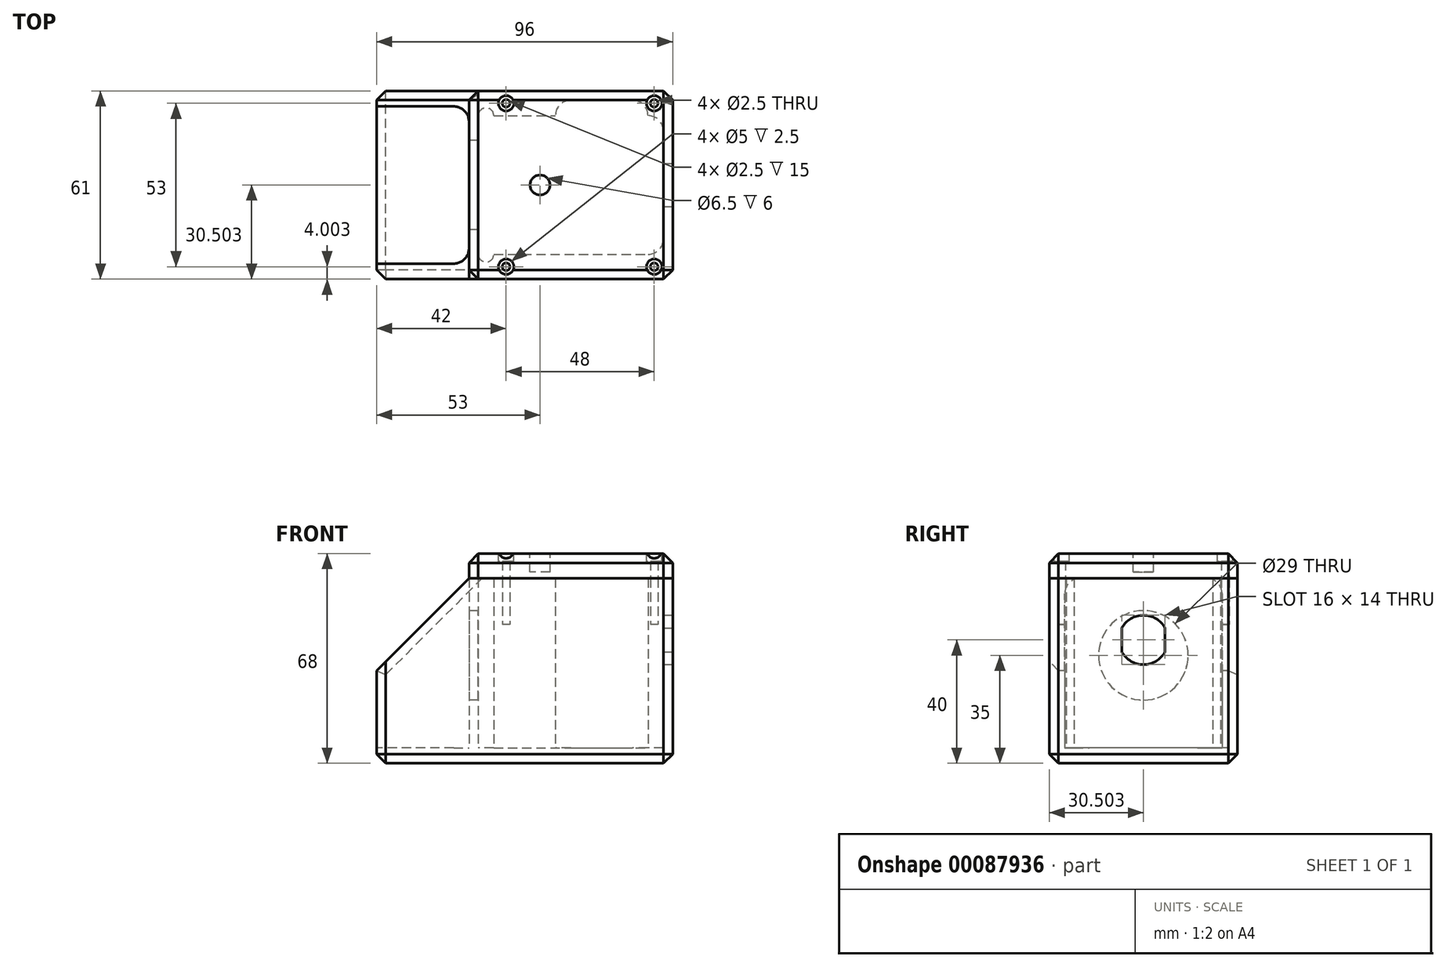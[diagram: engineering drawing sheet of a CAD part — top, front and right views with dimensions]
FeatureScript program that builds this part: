
annotation { "Feature Type Name" : "Feature", "Feature Type Description" : "" }
export const myFeature = defineFeature(function(context is Context, id is Id, definition is map)
    precondition{}
    {
        {
            var Q0;
            Q0=qCreatedBy(makeId("Top.planeOp"),FACE);
            var sketch = newSketch(context, id + "F0", { "sketchPlane" : qUnion([Q0])});
            skLineSegment(sketch, "E0.bottom", {"start": v(10, 29.15) * mm, "end": v(30, 29.15) * mm});
            skLineSegment(sketch, "E0.top", {"start": v(-15, -20.85) * mm, "end": v(35, -20.85) * mm});
            skLineSegment(sketch, "E0.left", {"start": v(-20, 24.15) * mm, "end": v(-20, -20.85) * mm});
            skLineSegment(sketch, "E0.right", {"start": v(40, 19.15) * mm, "end": v(40, -15.85) * mm});
            skLineSegment(sketch, "E1.0", {"start": v(-15, 24.15) * mm, "end": v(-10.83, 24.15) * mm, "construction": true});
            skLineSegment(sketch, "E2.0", {"start": v(5, 29.15) * mm, "end": v(5, -20.85) * mm, "construction": true});
            skLineSegment(sketch, "E3", {"start": v(5, 24.15) * mm, "end": v(5, 24.15) * mm});
            skLineSegment(sketch, "E4.bottom", {"start": v(43, 32.15) * mm, "end": v(-23, 32.15) * mm});
            skLineSegment(sketch, "E4.top", {"start": v(43, -28.85) * mm, "end": v(-23, -28.85) * mm});
            skLineSegment(sketch, "E4.left", {"start": v(43, 32.15) * mm, "end": v(43, -28.85) * mm});
            skLineSegment(sketch, "E4.right", {"start": v(-23, 32.15) * mm, "end": v(-23, -28.85) * mm});
            skPoint(sketch, "E4.middle", {"position": v(10, 1.65) * mm});
            skPoint(sketch, "E4.middle.positionSnap0", {"position": v(-20, 1.65) * mm});
            skPoint(sketch, "E4.centerSnap0", {"position": v(-20, 1.65) * mm});
            skPoint(sketch, "E5.visualSharp", {"position": v(5, 29.15) * mm});
            skArc(sketch, "E5.filletArc", {"start": v(10, 29.15) * mm, "mid": v(6.46, 27.69) * mm, "end": v(5, 24.15) * mm});
            skPoint(sketch, "E6.visualSharp", {"position": v(40, 29.15) * mm});
            skPoint(sketch, "E7.visualSharp", {"position": v(40, -20.85) * mm});
            skArc(sketch, "E7.filletArc", {"start": v(35, -20.85) * mm, "mid": v(38.54, -19.38) * mm, "end": v(40, -15.85) * mm});
            skLineSegment(sketch, "E8.0", {"start": v(-15, 24.15) * mm, "end": v(-15, -20.85) * mm, "construction": true});
            skArc(sketch, "E9", {"start": v(-15, 24.15) * mm, "mid": v(-17.5, 26.65) * mm, "end": v(-20, 24.15) * mm});
            skArc(sketch, "E10", {"start": v(-20, -20.85) * mm, "mid": v(-17.5, -23.35) * mm, "end": v(-15, -20.85) * mm});
            skLineSegment(sketch, "E11.trimOffspring", {"start": v(-15, 24.15) * mm, "end": v(5, 24.15) * mm});
            skLineSegment(sketch, "E12.bottom", {"start": v(-23, 32.15) * mm, "end": v(-53, 32.15) * mm});
            skLineSegment(sketch, "E12.top", {"start": v(-23, -28.85) * mm, "end": v(-53, -28.85) * mm});
            skLineSegment(sketch, "E12.right", {"start": v(-53, 32.15) * mm, "end": v(-53, -28.85) * mm});
            skLineSegment(sketch, "E13.0", {"start": v(-23, 27.15) * mm, "end": v(-53, 27.15) * mm});
            skLineSegment(sketch, "E14.0", {"start": v(-23, -23.85) * mm, "end": v(-53, -23.85) * mm});
            skLineSegment(sketch, "E15.top", {"start": v(35, 24.15) * mm, "end": v(35, 24.15) * mm});
            skLineSegment(sketch, "E15.right", {"start": v(35, 24.15) * mm, "end": v(35, 24.15) * mm});
            skArc(sketch, "E16.filletArc", {"start": v(35, 24.15) * mm, "mid": v(33.54, 27.69) * mm, "end": v(30, 29.15) * mm});
            skPoint(sketch, "E17.visualSharp", {"position": v(40, 24.15) * mm});
            skArc(sketch, "E17.filletArc", {"start": v(40, 19.15) * mm, "mid": v(38.54, 22.69) * mm, "end": v(35, 24.15) * mm});
            skLineSegment(sketch, "E18.0", {"start": v(43, 28.15) * mm, "end": v(-23, 28.15) * mm, "construction": true});
            skLineSegment(sketch, "E19.0", {"start": v(-11, 32.15) * mm, "end": v(-11, -28.85) * mm, "construction": true});
            skCircle(sketch, "E20", {"center": v(-11, 28.15) * mm, "radius": 1.25 * mm});
            skCircle(sketch, "E21.0.1.0", {"center": v(-11, -24.85) * mm, "radius": 1.25 * mm});
            skCircle(sketch, "E21.1.0.0", {"center": v(37, 28.15) * mm, "radius": 1.25 * mm});
            skCircle(sketch, "E21.1.1.0", {"center": v(37, -24.85) * mm, "radius": 1.25 * mm});
            skLineSegment(sketch, "E21.direction1", {"start": v(-11, 28.15) * mm, "end": v(37, 28.15) * mm, "construction": true});
            skLineSegment(sketch, "E21.direction2", {"start": v(-11, 28.15) * mm, "end": v(-11, -24.85) * mm, "construction": true});
            skSolve(sketch);
        }
        {
            var Q0;
            Q0=makeQuery(id+"F0.imprint","IMPRINT",FACE,{"disambiguationData":[TD([[makeQuery(id+"F0.imprint","IMPRINT",EDGE,{"derivedFrom":sQuery(id+"F0.wireOp",EDGE,"E0.bottom")}),1.0]])]});
            var Q1;
            {var subQ0=sQuery(id+"F0.wireOp",EDGE,"E12.bottom");Q1=makeQuery(id+"F0.imprint","IMPRINT",FACE,{"disambiguationData":[TD([[makeQuery(id+"F0.imprint","IMPRINT",EDGE,{"derivedFrom":subQ0}),1.0]])]});}
            var Q2;
            {var subQ0=sQuery(id+"F0.wireOp",EDGE,"E12.top");Q2=makeQuery(id+"F0.imprint","IMPRINT",FACE,{"disambiguationData":[TD([[makeQuery(id+"F0.imprint","IMPRINT",EDGE,{"derivedFrom":subQ0}),-1.0]])]});}
            extrude(context, id + "F1", {"entities" : qUnion([Q0, Q1, Q2]), "depth" : 55 * mm});
        }
        {
            var Q0;
            Q0=makeQuery(id+"F0.imprint","IMPRINT",FACE,{"disambiguationData":[TD([[makeQuery(id+"F0.imprint","IMPRINT",EDGE,{"derivedFrom":sQuery(id+"F0.wireOp",EDGE,"E20")}),1.0]])]});
            var Q1;
            Q1=makeQuery(id+"F0.imprint","IMPRINT",FACE,{"disambiguationData":[TD([[makeQuery(id+"F0.imprint","IMPRINT",EDGE,{"derivedFrom":sQuery(id+"F0.wireOp",EDGE,"E21.0.1.0")}),1.0]])]});
            var Q2;
            Q2=makeQuery(id+"F0.imprint","IMPRINT",FACE,{"disambiguationData":[TD([[makeQuery(id+"F0.imprint","IMPRINT",EDGE,{"derivedFrom":sQuery(id+"F0.wireOp",EDGE,"E21.1.1.0")}),1.0]])]});
            var Q3;
            Q3=makeQuery(id+"F0.imprint","IMPRINT",FACE,{"disambiguationData":[TD([[makeQuery(id+"F0.imprint","IMPRINT",EDGE,{"derivedFrom":sQuery(id+"F0.wireOp",EDGE,"E21.1.0.0")}),1.0]])]});
            extrude(context, id + "F2", {"entities" : qUnion([Q0, Q1, Q2, Q3]), "operationType" : NewBodyOperationType.ADD, "depth" : 40 * mm});
        }
        {
            var Q0;
            Q0 = qSketchRegion(id + "F0", true);
            var Q1;
            Q1=makeQuery(id+"F0.imprint","IMPRINT",FACE,{"disambiguationData":[TD([[makeQuery(id+"F0.imprint","IMPRINT",EDGE,{"derivedFrom":sQuery(id+"F0.wireOp",EDGE,"E0.bottom")}),-1.0]])]});
            var Q2;
            Q2=makeQuery(id+"F0.imprint","IMPRINT",FACE,{"disambiguationData":[TD([[makeQuery(id+"F0.imprint","IMPRINT",EDGE,{"derivedFrom":sQuery(id+"F0.wireOp",EDGE,"E20")}),1.0]])]});
            var Q3;
            Q3=makeQuery(id+"F0.imprint","IMPRINT",FACE,{"disambiguationData":[TD([[makeQuery(id+"F0.imprint","IMPRINT",EDGE,{"derivedFrom":sQuery(id+"F0.wireOp",EDGE,"E21.0.1.0")}),1.0]])]});
            var Q4;
            Q4=makeQuery(id+"F0.imprint","IMPRINT",FACE,{"disambiguationData":[TD([[makeQuery(id+"F0.imprint","IMPRINT",EDGE,{"derivedFrom":sQuery(id+"F0.wireOp",EDGE,"E21.1.0.0")}),1.0]])]});
            var Q5;
            Q5=makeQuery(id+"F0.imprint","IMPRINT",FACE,{"disambiguationData":[TD([[makeQuery(id+"F0.imprint","IMPRINT",EDGE,{"derivedFrom":sQuery(id+"F0.wireOp",EDGE,"E21.1.1.0")}),1.0]])]});
            extrude(context, id + "F3", {"entities" : qUnion([Q0, Q1, Q2, Q3, Q4, Q5]), "operationType" : NewBodyOperationType.ADD, "oppositeDirection" : true, "depth" : 5 * mm});
        }
        {
            var Q0;
            {var subQ0=sQuery(id+"F0.wireOp",EDGE,"E12.top");var subQ1=sQuery(id+"F0.wireOp",EDGE,"E4.top");Q0=makeQuery(id+"F3.boolean.opBoolean","MERGE",FACE,{"derivedFrom":[makeQuery(id+"F1.opExtrude","SWEPT_FACE",FACE,{"disambiguationData":[OSD([subQ1,subQ0])]}),makeQuery(id+"F3.opExtrude","SWEPT_FACE",FACE,{"disambiguationData":[OSD([subQ1,subQ0])]})]});}
            var sketch = newSketch(context, id + "F4", { "sketchPlane" : qUnion([Q0])});
            skLineSegment(sketch, "E22.0", {"start": v(43, 40) * mm, "end": v(-53, 40) * mm, "construction": true});
            skLineSegment(sketch, "E23.0", {"start": v(-48, 55) * mm, "end": v(-48, -5) * mm, "construction": true});
            skLineSegment(sketch, "E24", {"start": v(-53, 25) * mm, "end": v(-23, 55) * mm});
            skSolve(sketch);
        }
        {
            var Q0;
            {var subQ0=sQuery(id+"F4.wireOp",EDGE,"E24");Q0=makeQuery(id+"F4.imprint","IMPRINT",FACE,{"disambiguationData":[TD([[makeQuery(id+"F4.imprint","IMPRINT",EDGE,{"derivedFrom":subQ0}),1.0]])]});}
            extrude(context, id + "F5", {"entities" : qUnion([Q0]), "operationType" : NewBodyOperationType.REMOVE, "endBound" : BoundingType.THROUGH_ALL, "oppositeDirection" : true, "depth" : 25 * mm});
        }
        {
            var Q0;
            Q0=makeQuery(id+"F1.opExtrude","CAP_FACE",FACE,{"disambiguationData":[OSD([sQuery(id+"F0.wireOp",EDGE,"E0.bottom"),sQuery(id+"F0.wireOp",EDGE,"E0.top"),sQuery(id+"F0.wireOp",EDGE,"E0.left"),sQuery(id+"F0.wireOp",EDGE,"E0.right"),sQuery(id+"F0.wireOp",EDGE,"E4.bottom"),sQuery(id+"F0.wireOp",EDGE,"E4.top"),sQuery(id+"F0.wireOp",EDGE,"E4.left"),sQuery(id+"F0.wireOp",EDGE,"E5.filletArc"),sQuery(id+"F0.wireOp",EDGE,"E6.filletArc"),sQuery(id+"F0.wireOp",EDGE,"E7.filletArc"),sQuery(id+"F0.wireOp",EDGE,"E9"),sQuery(id+"F0.wireOp",EDGE,"E10"),sQuery(id+"F0.wireOp",EDGE,"E11.trimOffspring"),sQuery(id+"F0.wireOp",EDGE,"E12.bottom"),sQuery(id+"F0.wireOp",EDGE,"E12.top"),sQuery(id+"F0.wireOp",EDGE,"E4.right"),sQuery(id+"F0.wireOp",EDGE,"E12.right"),sQuery(id+"F0.wireOp",EDGE,"E13.0"),sQuery(id+"F0.wireOp",EDGE,"E14.0")])],"isStart":false});
            var sketch = newSketch(context, id + "F6", { "sketchPlane" : qUnion([Q0])});
            skLineSegment(sketch, "E25.0.0", {"start": v(43, 32.15) * mm, "end": v(-23, 32.15) * mm});
            skLineSegment(sketch, "E25.0.1", {"start": v(-23, 32.15) * mm, "end": v(-23, 27.15) * mm});
            skLineSegment(sketch, "E25.0.2", {"start": v(-23, 27.15) * mm, "end": v(-23, -23.85) * mm});
            skLineSegment(sketch, "E25.0.3", {"start": v(-23, -23.85) * mm, "end": v(-23, -28.85) * mm});
            skLineSegment(sketch, "E25.0.4", {"start": v(-23, -28.85) * mm, "end": v(43, -28.85) * mm});
            skLineSegment(sketch, "E25.0.5", {"start": v(43, -28.85) * mm, "end": v(43, 32.15) * mm});
            skSolve(sketch);
        }
        {
            var Q0;
            Q0=makeQuery(id+"F6.imprint","IMPRINT",FACE,{"disambiguationData":[TD([[makeQuery(id+"F6.imprint","IMPRINT",EDGE,{"derivedFrom":makeQuery(id+"F1.opExtrude","CAP_EDGE",EDGE,{"disambiguationData":[OSD([sQuery(id+"F0.wireOp",EDGE,"E0.bottom")])],"isStart":false})}),-1.0]])]});
            var Q1;
            Q1=makeQuery(id+"F6.imprint","IMPRINT",FACE,{"disambiguationData":[TD([[makeQuery(id+"F6.imprint","IMPRINT",EDGE,{"derivedFrom":sQuery(id+"F6.wireOp",EDGE,"E25.0.0")}),1.0]])]});
            extrude(context, id + "F7", {"entities" : qUnion([Q0, Q1]), "depth" : 8 * mm});
        }
        {
            var Q0;
            {var subQ0=sQuery(id+"F0.wireOp",EDGE,"E4.left");Q0=makeQuery(id+"F3.boolean.opBoolean","MERGE",FACE,{"derivedFrom":[makeQuery(id+"F1.opExtrude","SWEPT_FACE",FACE,{"disambiguationData":[OSD([subQ0])]}),makeQuery(id+"F3.opExtrude","SWEPT_FACE",FACE,{"disambiguationData":[OSD([subQ0])]})]});}
            var sketch = newSketch(context, id + "F8", { "sketchPlane" : qUnion([Q0])});
            skCircle(sketch, "E26", {"center": v(1.65, 35) * mm, "radius": 8 * mm});
            skPoint(sketch, "E26.centerSnap0", {"position": v(1.65, 55) * mm});
            skLineSegment(sketch, "E27", {"start": v(-5.35, 47.17) * mm, "end": v(-5.35, 23) * mm, "construction": true});
            skLineSegment(sketch, "E28", {"start": v(8.65, 47.17) * mm, "end": v(8.65, 23) * mm, "construction": true});
            skLineSegment(sketch, "E29", {"start": v(-5.35, 38.87) * mm, "end": v(-5.35, 31.13) * mm});
            skLineSegment(sketch, "E30", {"start": v(8.65, 31.13) * mm, "end": v(8.65, 38.87) * mm});
            skSolve(sketch);
        }
        {
            var Q0;
            {var subQ0=sQuery(id+"F8.wireOp",EDGE,"E29");Q0=makeQuery(id+"F8.imprint","IMPRINT",FACE,{"disambiguationData":[TD([[makeQuery(id+"F8.imprint","IMPRINT",EDGE,{"derivedFrom":subQ0}),1.0]])]});}
            extrude(context, id + "F9", {"entities" : qUnion([Q0]), "operationType" : NewBodyOperationType.REMOVE, "endBound" : BoundingType.UP_TO_NEXT, "oppositeDirection" : true, "depth" : 25 * mm});
        }
        {
            var Q0;
            Q0=makeQuery(id+"F7.opExtrude","CAP_FACE",FACE,{"disambiguationData":[OSD([sQuery(id+"F0.wireOp",EDGE,"E20"),sQuery(id+"F0.wireOp",EDGE,"E21.0.1.0"),sQuery(id+"F0.wireOp",EDGE,"E21.1.0.0"),sQuery(id+"F0.wireOp",EDGE,"E21.1.1.0"),sQuery(id+"F6.wireOp",EDGE,"E25.0.0"),sQuery(id+"F6.wireOp",EDGE,"E25.0.1"),sQuery(id+"F6.wireOp",EDGE,"E25.0.2"),sQuery(id+"F6.wireOp",EDGE,"E25.0.3"),sQuery(id+"F6.wireOp",EDGE,"E25.0.4"),sQuery(id+"F6.wireOp",EDGE,"E25.0.5")])],"isStart":false});
            var sketch = newSketch(context, id + "F10", { "sketchPlane" : qUnion([Q0])});
            skCircle(sketch, "E31", {"center": v(-11, 28.15) * mm, "radius": 2.5 * mm});
            skCircle(sketch, "E32.0.1.0", {"center": v(-11, -24.85) * mm, "radius": 2.5 * mm});
            skCircle(sketch, "E32.1.0.0", {"center": v(37, 28.15) * mm, "radius": 2.5 * mm});
            skCircle(sketch, "E32.1.1.0", {"center": v(37, -24.85) * mm, "radius": 2.5 * mm});
            skLineSegment(sketch, "E32.direction1", {"start": v(-11, 28.15) * mm, "end": v(37, 28.15) * mm, "construction": true});
            skLineSegment(sketch, "E32.direction2", {"start": v(-11, 28.15) * mm, "end": v(-11, -24.85) * mm, "construction": true});
            skSolve(sketch);
        }
        {
            var Q0;
            Q0=makeQuery(id+"F10.imprint","IMPRINT",FACE,{"disambiguationData":[TD([[makeQuery(id+"F10.imprint","IMPRINT",EDGE,{"derivedFrom":sQuery(id+"F10.wireOp",EDGE,"E31")}),1.0]])]});
            var Q1;
            Q1=makeQuery(id+"F10.imprint","IMPRINT",FACE,{"disambiguationData":[TD([[makeQuery(id+"F10.imprint","IMPRINT",EDGE,{"derivedFrom":sQuery(id+"F10.wireOp",EDGE,"E32.1.0.0")}),1.0]])]});
            var Q2;
            Q2=makeQuery(id+"F10.imprint","IMPRINT",FACE,{"disambiguationData":[TD([[makeQuery(id+"F10.imprint","IMPRINT",EDGE,{"derivedFrom":sQuery(id+"F10.wireOp",EDGE,"E32.0.1.0")}),1.0]])]});
            var Q3;
            Q3=makeQuery(id+"F10.imprint","IMPRINT",FACE,{"disambiguationData":[TD([[makeQuery(id+"F10.imprint","IMPRINT",EDGE,{"derivedFrom":sQuery(id+"F10.wireOp",EDGE,"E32.1.1.0")}),1.0]])]});
            extrude(context, id + "F11", {"entities" : qUnion([Q0, Q1, Q2, Q3]), "operationType" : NewBodyOperationType.REMOVE, "oppositeDirection" : true, "depth" : 2.5 * mm});
        }
        {
            var Q0;
            Q0=makeQuery(id+"F7.opExtrude","CAP_EDGE",EDGE,{"disambiguationData":[OSD([sQuery(id+"F6.wireOp",EDGE,"E25.0.4")])],"isStart":false});
            var Q1;
            Q1=makeQuery(id+"F7.opExtrude","CAP_EDGE",EDGE,{"disambiguationData":[OSD([sQuery(id+"F6.wireOp",EDGE,"E25.0.5")])],"isStart":false});
            var Q2;
            Q2=makeQuery(id+"F7.opExtrude","CAP_EDGE",EDGE,{"disambiguationData":[OSD([sQuery(id+"F6.wireOp",EDGE,"E25.0.0")])],"isStart":false});
            var Q3;
            Q3=makeQuery(id+"F7.opExtrude","CAP_EDGE",EDGE,{"disambiguationData":[OSD([sQuery(id+"F6.wireOp",EDGE,"E25.0.1"),sQuery(id+"F6.wireOp",EDGE,"E25.0.2"),sQuery(id+"F6.wireOp",EDGE,"E25.0.3")])],"isStart":false});
            var Q4;
            {var subQ0=sQuery(id+"F0.wireOp",EDGE,"E4.left");var subQ1=sQuery(id+"F0.wireOp",EDGE,"E4.top");Q4=makeQuery(id+"F3.boolean.opBoolean","MERGE",EDGE,{"derivedFrom":[makeQuery(id+"F1.opExtrude","SWEPT_EDGE",EDGE,{"disambiguationData":[OSD([subQ1,subQ0])]}),makeQuery(id+"F3.opExtrude","SWEPT_EDGE",EDGE,{"disambiguationData":[OSD([subQ1,subQ0])]})]});}
            var Q5;
            Q5=makeQuery(id+"F7.opExtrude","SWEPT_EDGE",EDGE,{"disambiguationData":[OSD([sQuery(id+"F6.wireOp",EDGE,"E25.0.4"),sQuery(id+"F6.wireOp",EDGE,"E25.0.5")])]});
            var Q6;
            Q6=makeQuery(id+"F7.opExtrude","SWEPT_EDGE",EDGE,{"disambiguationData":[OSD([sQuery(id+"F6.wireOp",EDGE,"E25.0.0"),sQuery(id+"F6.wireOp",EDGE,"E25.0.5")])]});
            var Q7;
            {var subQ0=sQuery(id+"F0.wireOp",EDGE,"E4.left");var subQ1=sQuery(id+"F0.wireOp",EDGE,"E4.bottom");Q7=makeQuery(id+"F3.boolean.opBoolean","MERGE",EDGE,{"derivedFrom":[makeQuery(id+"F1.opExtrude","SWEPT_EDGE",EDGE,{"disambiguationData":[OSD([subQ1,subQ0])]}),makeQuery(id+"F3.opExtrude","SWEPT_EDGE",EDGE,{"disambiguationData":[OSD([subQ1,subQ0])]})]});}
            var Q8;
            Q8=makeQuery(id+"F7.opExtrude","SWEPT_EDGE",EDGE,{"disambiguationData":[OSD([sQuery(id+"F6.wireOp",EDGE,"E25.0.0"),sQuery(id+"F6.wireOp",EDGE,"E25.0.1")])]});
            var Q9;
            {var subQ0=sQuery(id+"F0.wireOp",EDGE,"E12.bottom");var subQ1=sQuery(id+"F0.wireOp",EDGE,"E4.bottom");Q9=makeQuery(id+"F5.boolean.opBoolean","INTERSECT",EDGE,{"derivedFrom":[makeQuery(id+"F3.boolean.opBoolean","MERGE",FACE,{"derivedFrom":[makeQuery(id+"F1.opExtrude","SWEPT_FACE",FACE,{"disambiguationData":[OSD([subQ1,subQ0])]}),makeQuery(id+"F3.opExtrude","SWEPT_FACE",FACE,{"disambiguationData":[OSD([subQ1,subQ0])]})]}),makeQuery(id+"F5.opExtrude","SWEPT_FACE",FACE,{"disambiguationData":[OSD([sQuery(id+"F4.wireOp",EDGE,"E24")])]})]});}
            var Q10;
            {var subQ0=sQuery(id+"F0.wireOp",EDGE,"E12.right");var subQ1=sQuery(id+"F0.wireOp",EDGE,"E12.bottom");Q10=makeQuery(id+"F3.boolean.opBoolean","MERGE",EDGE,{"derivedFrom":[makeQuery(id+"F1.opExtrude","SWEPT_EDGE",EDGE,{"disambiguationData":[OSD([subQ1,subQ0])]}),makeQuery(id+"F3.opExtrude","SWEPT_EDGE",EDGE,{"disambiguationData":[OSD([subQ1,subQ0])]})]});}
            var Q11;
            Q11=makeQuery(id+"F3.opExtrude","CAP_EDGE",EDGE,{"disambiguationData":[OSD([sQuery(id+"F0.wireOp",EDGE,"E4.bottom"),sQuery(id+"F0.wireOp",EDGE,"E12.bottom")])],"isStart":false});
            var Q12;
            Q12=makeQuery(id+"F3.opExtrude","CAP_EDGE",EDGE,{"disambiguationData":[OSD([sQuery(id+"F0.wireOp",EDGE,"E12.right")])],"isStart":false});
            var Q13;
            {var subQ0=sQuery(id+"F0.wireOp",EDGE,"E12.right");var subQ1=sQuery(id+"F0.wireOp",EDGE,"E12.top");Q13=makeQuery(id+"F3.boolean.opBoolean","MERGE",EDGE,{"derivedFrom":[makeQuery(id+"F1.opExtrude","SWEPT_EDGE",EDGE,{"disambiguationData":[OSD([subQ1,subQ0])]}),makeQuery(id+"F3.opExtrude","SWEPT_EDGE",EDGE,{"disambiguationData":[OSD([subQ1,subQ0])]})]});}
            var Q14;
            Q14=makeQuery(id+"F5.boolean.opBoolean","COPY",EDGE,{"derivedFrom":makeQuery(id+"F5.opExtrude","CAP_EDGE",EDGE,{"disambiguationData":[OSD([sQuery(id+"F4.wireOp",EDGE,"E24")])],"isStart":true})});
            var Q15;
            Q15=makeQuery(id+"F7.opExtrude","SWEPT_EDGE",EDGE,{"disambiguationData":[OSD([sQuery(id+"F6.wireOp",EDGE,"E25.0.3"),sQuery(id+"F6.wireOp",EDGE,"E25.0.4")])]});
            var Q16;
            Q16=makeQuery(id+"F3.opExtrude","CAP_EDGE",EDGE,{"disambiguationData":[OSD([sQuery(id+"F0.wireOp",EDGE,"E4.left")])],"isStart":false});
            var Q17;
            Q17=makeQuery(id+"F3.opExtrude","CAP_EDGE",EDGE,{"disambiguationData":[OSD([sQuery(id+"F0.wireOp",EDGE,"E4.top"),sQuery(id+"F0.wireOp",EDGE,"E12.top")])],"isStart":false});
            chamfer(context, id + "F12", {"entities" : qUnion([Q0, Q1, Q2, Q3, Q4, Q5, Q6, Q7, Q8, Q9, Q10, Q11, Q12, Q13, Q14, Q15, Q16, Q17]), "width" : 3 * mm, "tangentPropagation" : true});
        }
        {
            var Q0;
            Q0=makeQuery(id+"F1.opExtrude","SWEPT_EDGE",EDGE,{"disambiguationData":[OSD([sQuery(id+"F0.wireOp",EDGE,"E4.right"),sQuery(id+"F0.wireOp",EDGE,"E13.0")])]});
            var Q1;
            Q1=makeQuery(id+"F1.opExtrude","SWEPT_EDGE",EDGE,{"disambiguationData":[OSD([sQuery(id+"F0.wireOp",EDGE,"E4.right"),sQuery(id+"F0.wireOp",EDGE,"E14.0")])]});
            fillet(context, id + "F13", {"entities" : qUnion([Q0, Q1]), "radius" : 5 * mm, "tangentPropagation" : true, "allowEdgeOverflow" : false});
        }
        {
            var Q0;
            Q0=makeQuery(id+"F1.opExtrude","SWEPT_FACE",FACE,{"disambiguationData":[OSD([sQuery(id+"F0.wireOp",EDGE,"E4.right")])]});
            var sketch = newSketch(context, id + "F14", { "sketchPlane" : qUnion([Q0])});
            skCircle(sketch, "E33", {"center": v(-1.65, 30) * mm, "radius": 14.5 * mm});
            skPoint(sketch, "E33.centerSnap0", {"position": v(-1.65, 55) * mm});
            skSolve(sketch);
        }
        {
            var Q0;
            Q0=makeQuery(id+"F14.imprint","IMPRINT",FACE,{"disambiguationData":[TD([[makeQuery(id+"F14.imprint","IMPRINT",EDGE,{"derivedFrom":sQuery(id+"F14.wireOp",EDGE,"E33")}),1.0]])]});
            extrude(context, id + "F15", {"entities" : qUnion([Q0]), "operationType" : NewBodyOperationType.REMOVE, "endBound" : BoundingType.UP_TO_NEXT, "oppositeDirection" : true, "depth" : 25 * mm});
        }
        {
            var Q0;
            Q0=makeQuery(id+"F7.opExtrude","CAP_FACE",FACE,{"disambiguationData":[OSD([sQuery(id+"F0.wireOp",EDGE,"E20"),sQuery(id+"F0.wireOp",EDGE,"E21.0.1.0"),sQuery(id+"F0.wireOp",EDGE,"E21.1.0.0"),sQuery(id+"F0.wireOp",EDGE,"E21.1.1.0"),sQuery(id+"F6.wireOp",EDGE,"E25.0.0"),sQuery(id+"F6.wireOp",EDGE,"E25.0.1"),sQuery(id+"F6.wireOp",EDGE,"E25.0.2"),sQuery(id+"F6.wireOp",EDGE,"E25.0.3"),sQuery(id+"F6.wireOp",EDGE,"E25.0.4"),sQuery(id+"F6.wireOp",EDGE,"E25.0.5")])],"isStart":false});
            var sketch = newSketch(context, id + "F16", { "sketchPlane" : qUnion([Q0])});
            skCircle(sketch, "E34", {"center": v(0, 1.65) * mm, "radius": 3.25 * mm});
            skPoint(sketch, "E34.centerSnap0", {"position": v(40, 1.65) * mm});
            skSolve(sketch);
        }
        {
            var Q0;
            Q0 = qSketchRegion(id + "F16", true);
            var Q1;
            Q1=makeQuery(id+"F16.imprint","IMPRINT",FACE,{"disambiguationData":[TD([[makeQuery(id+"F16.imprint","IMPRINT",EDGE,{"derivedFrom":sQuery(id+"F16.wireOp",EDGE,"E34")}),1.0]])]});
            extrude(context, id + "F17", {"entities" : qUnion([Q0, Q1]), "operationType" : NewBodyOperationType.REMOVE, "oppositeDirection" : true, "depth" : 6 * mm});
        }
    });
